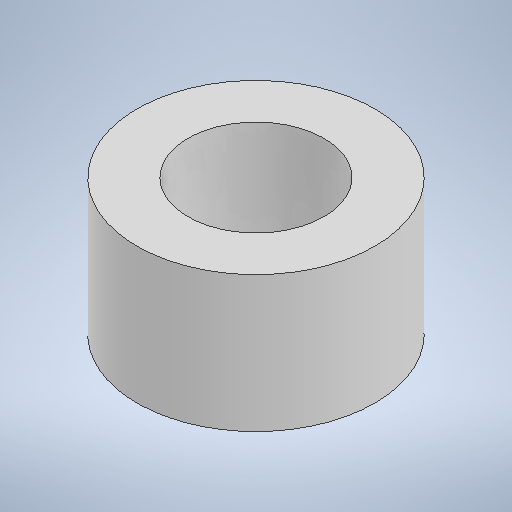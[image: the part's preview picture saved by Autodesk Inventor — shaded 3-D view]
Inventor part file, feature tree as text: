
AUTODESK INVENTOR PART (.ipt)
format: ipt  version: 2025.1 (Build 291241000, 241)  size: 212,992 bytes
history: native  units: mm
features: sketch x2, extrude x1, plane x1, hole x1
ambient origin geometry x8: Origin, YZ Plane, XZ Plane, XY Plane, X Axis, Y Axis, Z Axis, Center Point
bodies: Solid1 (feature_tree)
feature tree (5):
  extrude  "Extrusion1"  Depth=8.0mm
  plane  "Work Plane1"
  hole  "Hole1"  [1 undecoded]
  sketch  "Sketch1"  dims[d0=14.0mm d1=8.0mm]
  sketch  "Sketch2"  dims[d2=8.0mm d3=0.0mm d4=7.0mm d5=6.0mm d6=6.0mm d7=4.0mm d8=2.0mm d9=90.0deg d10=2.5mm d11=0.0mm]
note: 1 required parameter value undecoded (feature->parameter linkage not recoverable at this tier; creation-order binding heuristic only, values carry confidence <= 0.55)
